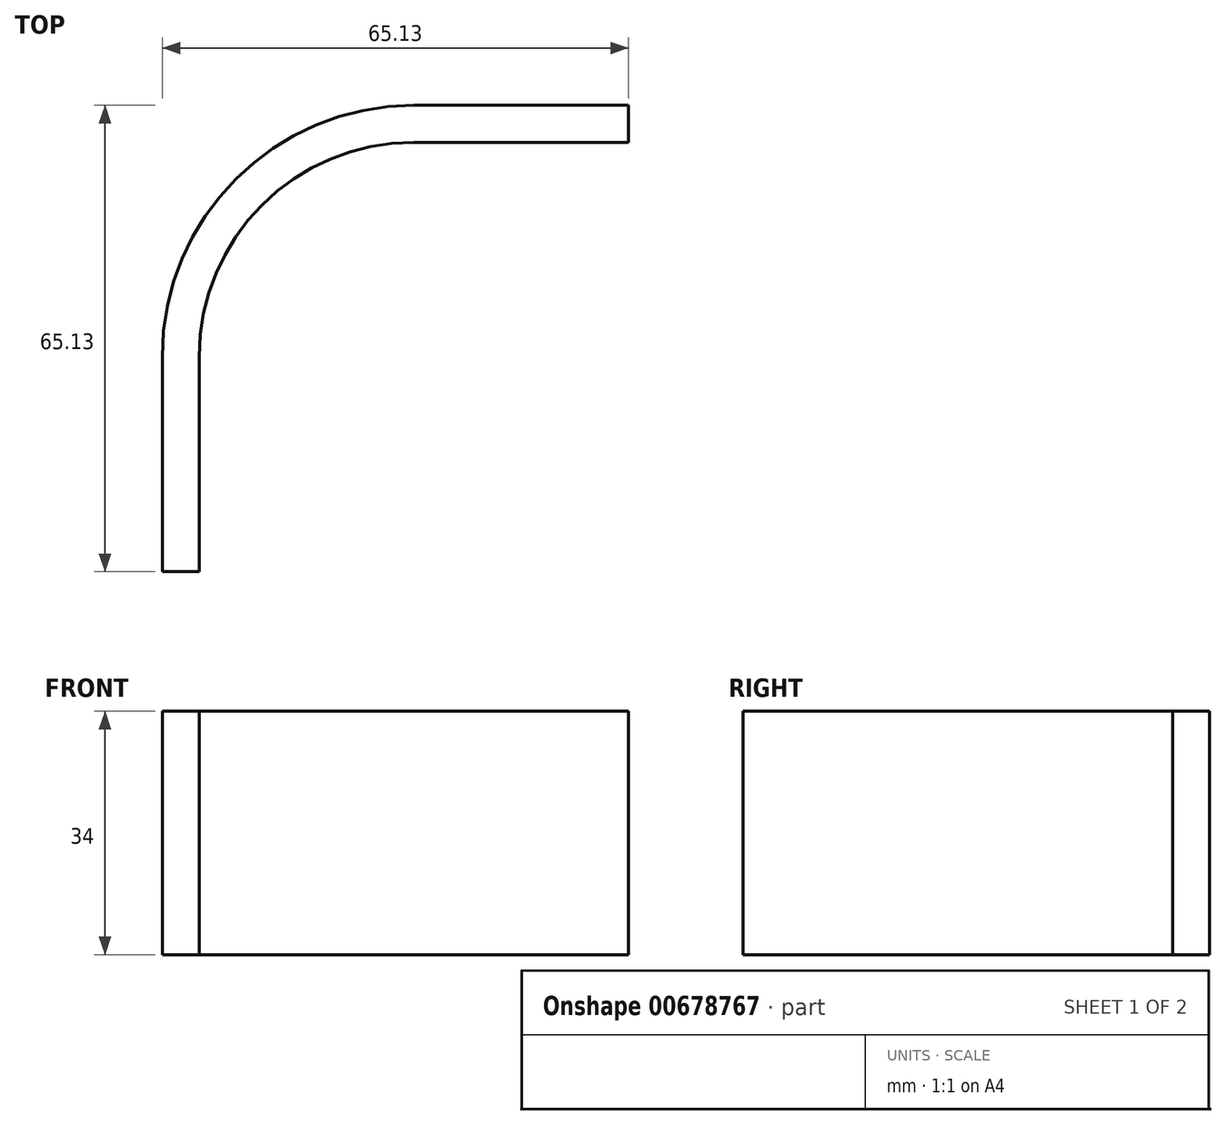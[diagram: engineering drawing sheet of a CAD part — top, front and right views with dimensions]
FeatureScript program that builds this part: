
annotation { "Feature Type Name" : "Feature", "Feature Type Description" : "" }
export const myFeature = defineFeature(function(context is Context, id is Id, definition is map)
    precondition{}
    {
        {
            var Q0;
            Q0=qCreatedBy(makeId("Top.planeOp"),FACE);
            var sketch = newSketch(context, id + "F0", { "sketchPlane" : qUnion([Q0])});
            skCircle(sketch, "E0", {"center": v(0, 0) * mm, "radius": 35.13 * mm});
            skCircle(sketch, "E1", {"center": v(0, 0) * mm, "radius": 29.98 * mm});
            skSolve(sketch);
        }
        {
            var Q0;
            Q0=makeQuery(id+"F0.imprint","IMPRINT",FACE,{"disambiguationData":[TD([[makeQuery(id+"F0.imprint","IMPRINT",EDGE,{"derivedFrom":sQuery(id+"F0.wireOp",EDGE,"E0")}),1.0]])]});
            var Q1;
            Q1 = qSketchRegion(id + "F2", true);
            extrude(context, id + "F1", {"entities" : qUnion([Q0, Q1]), "depth" : 34 * mm, "offsetDistance" : 25 * mm});
        }
        {
            var Q0;
            Q0=qCreatedBy(makeId("Top.planeOp"),FACE);
            var sketch = newSketch(context, id + "F2", { "sketchPlane" : qUnion([Q0])});
            skLineSegment(sketch, "E2.bottom", {"start": v(0, 0) * mm, "end": v(-44.66, 0) * mm});
            skLineSegment(sketch, "E2.top", {"start": v(0, -44.4) * mm, "end": v(-44.66, -44.4) * mm});
            skLineSegment(sketch, "E2.right", {"start": v(-44.66, 0) * mm, "end": v(-44.66, -44.4) * mm});
            skPoint(sketch, "E2.middle", {"position": v(-22.33, -22.2) * mm});
            skLineSegment(sketch, "E3.top", {"start": v(0, -49.63) * mm, "end": v(44.14, -49.63) * mm});
            skLineSegment(sketch, "E3.left", {"start": v(0, -44.4) * mm, "end": v(0, -49.63) * mm});
            skLineSegment(sketch, "E3.right", {"start": v(44.14, 0) * mm, "end": v(44.14, -49.63) * mm});
            skPoint(sketch, "E3.middle", {"position": v(22.07, -24.82) * mm});
            skLineSegment(sketch, "E4.bottom", {"start": v(44.14, 0) * mm, "end": v(47.8, 0) * mm});
            skLineSegment(sketch, "E4.top", {"start": v(0, 50.67) * mm, "end": v(47.8, 50.67) * mm});
            skLineSegment(sketch, "E4.left", {"start": v(0, 0) * mm, "end": v(0, 50.67) * mm});
            skLineSegment(sketch, "E4.right", {"start": v(47.8, 0) * mm, "end": v(47.8, 50.67) * mm});
            skPoint(sketch, "E4.middle", {"position": v(23.9, 25.33) * mm});
            skSolve(sketch);
        }
        {
            var Q0;
            Q0=makeQuery(id+"F2.imprint","IMPRINT",FACE,{"disambiguationData":[TD([[makeQuery(id+"F2.imprint","IMPRINT",EDGE,{"derivedFrom":sQuery(id+"F2.wireOp",EDGE,"E2.bottom")}),1.0]])]});
            extrude(context, id + "F3", {"entities" : qUnion([Q0]), "operationType" : NewBodyOperationType.REMOVE, "depth" : 56.7 * mm, "offsetDistance" : 25 * mm});
        }
        {
            var Q0;
            Q0=makeQuery(id+"F3.boolean.opBoolean","COPY",FACE,{"derivedFrom":makeQuery(id+"F3.opExtrude","SWEPT_FACE",FACE,{"disambiguationData":[OSD([sQuery(id+"F2.wireOp",EDGE,"E4.left")])]})});
            extrude(context, id + "F4", {"entities" : qUnion([Q0]), "operationType" : NewBodyOperationType.ADD, "depth" : 15 * mm, "offsetDistance" : 25 * mm});
        }
        {
            var Q0;
            Q0=makeQuery(id+"F3.boolean.opBoolean","COPY",FACE,{"derivedFrom":makeQuery(id+"F3.opExtrude","SWEPT_FACE",FACE,{"disambiguationData":[OSD([sQuery(id+"F2.wireOp",EDGE,"E2.bottom")])]})});
            extrude(context, id + "F5", {"entities" : qUnion([Q0]), "operationType" : NewBodyOperationType.ADD, "depth" : 15 * mm, "offsetDistance" : 25 * mm});
        }
        {
            var Q0;
            Q0=makeQuery(id+"F5.opExtrude","CAP_FACE",FACE,{"disambiguationData":[OSD([sQuery(id+"F2.wireOp",EDGE,"E2.bottom")])],"isStart":false});
            extrude(context, id + "F6", {"entities" : qUnion([Q0]), "operationType" : NewBodyOperationType.ADD, "depth" : 15 * mm, "offsetDistance" : 25 * mm});
        }
        {
            var Q0;
            Q0=makeQuery(id+"F4.opExtrude","CAP_FACE",FACE,{"disambiguationData":[OSD([sQuery(id+"F2.wireOp",EDGE,"E4.left")])],"isStart":false});
            extrude(context, id + "F7", {"entities" : qUnion([Q0]), "operationType" : NewBodyOperationType.ADD, "depth" : 15 * mm, "offsetDistance" : 25 * mm});
        }
    });
